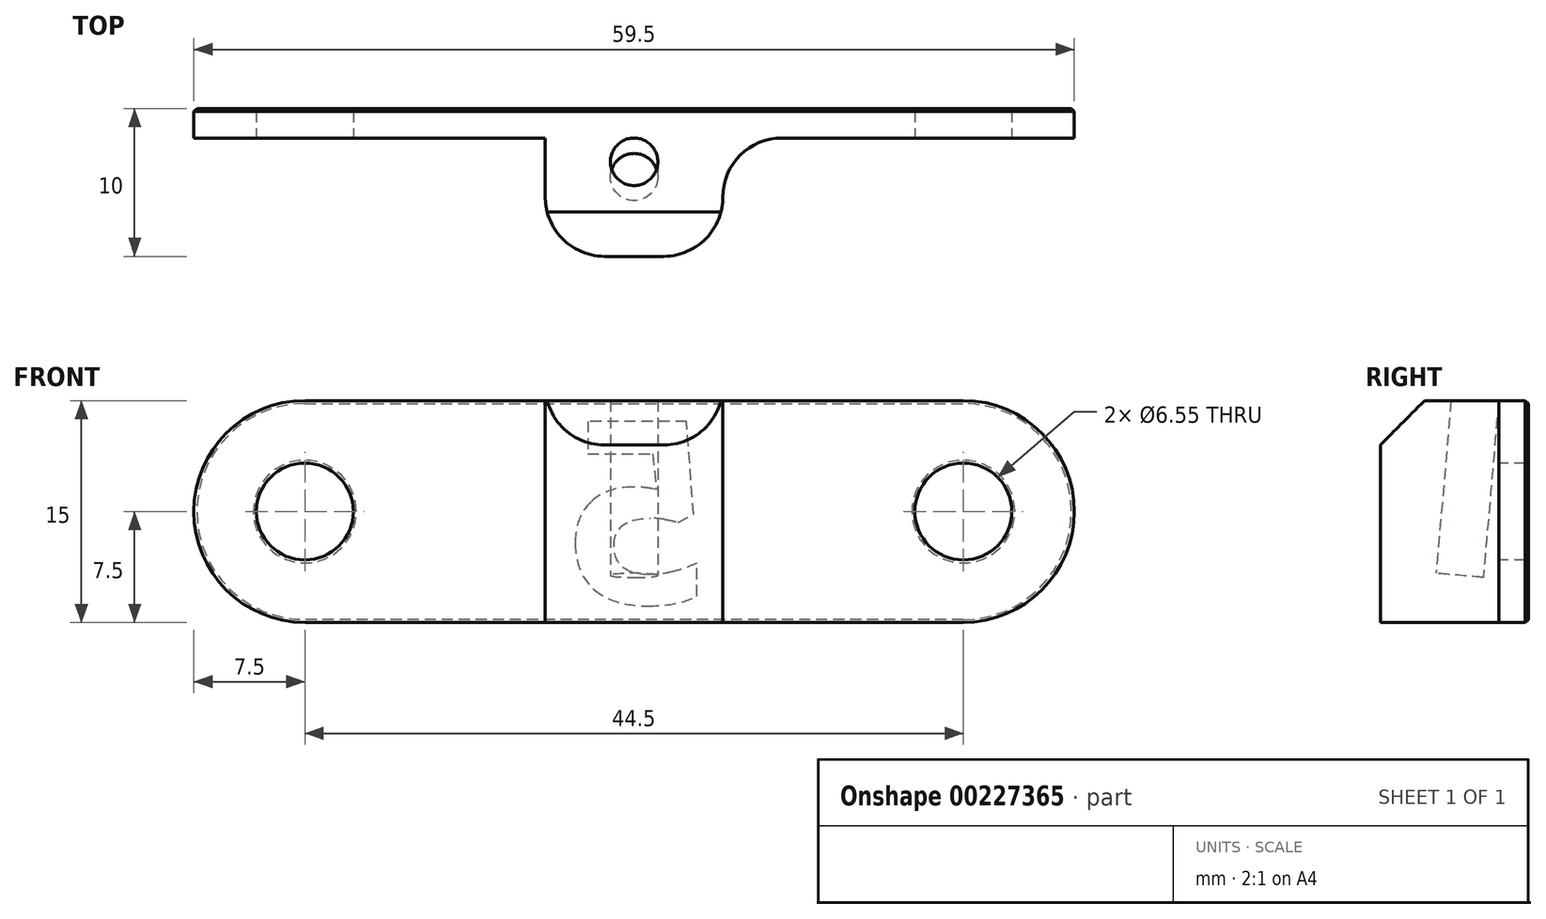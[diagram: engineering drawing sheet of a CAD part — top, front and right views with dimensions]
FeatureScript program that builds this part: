
annotation { "Feature Type Name" : "Feature", "Feature Type Description" : "" }
export const myFeature = defineFeature(function(context is Context, id is Id, definition is map)
    precondition{}
    {
        {
            var Q0;
            Q0=qCreatedBy(makeId("Front.planeOp"),FACE);
            var sketch = newSketch(context, id + "F0", { "sketchPlane" : qUnion([Q0])});
            skCircle(sketch, "E0", {"center": v(-22.25, 0) * mm, "radius": 3.28 * mm});
            skCircle(sketch, "E1", {"center": v(22.25, 0) * mm, "radius": 3.28 * mm});
            skLineSegment(sketch, "E2", {"start": v(-22.25, 0) * mm, "end": v(22.25, 0) * mm, "construction": true});
            skArc(sketch, "E3.0.startCap", {"start": v(-22.25, -7.5) * mm, "mid": v(-29.75, 0) * mm, "end": v(-22.25, 7.5) * mm});
            skArc(sketch, "E3.0.endCap", {"start": v(22.25, 7.5) * mm, "mid": v(29.75, 0) * mm, "end": v(22.25, -7.5) * mm});
            skLineSegment(sketch, "E3.0.left", {"start": v(-22.25, 7.5) * mm, "end": v(22.25, 7.5) * mm});
            skLineSegment(sketch, "E3.0.right", {"start": v(-22.25, -7.5) * mm, "end": v(22.25, -7.5) * mm});
            skSolve(sketch);
        }
        {
            var Q0;
            Q0=qSketchRegion(id+"F0",true);
            extrude(context, id + "F1", {"entities" : qUnion([Q0]), "oppositeDirection" : true, "depth" : 2 * mm, "offsetDistance" : 25 * mm});
        }
        {
            var Q0;
            Q0=qCreatedBy(makeId("Right.planeOp"),FACE);
            var sketch = newSketch(context, id + "F2", { "sketchPlane" : qUnion([Q0])});
            skLineSegment(sketch, "E4", {"start": v(-1.05, -4.45) * mm, "end": v(3, 41.76) * mm});
            skLineSegment(sketch, "E5", {"start": v(3, 41.76) * mm, "end": v(-0.2, 42.04) * mm});
            skLineSegment(sketch, "E6", {"start": v(-0.2, 42.04) * mm, "end": v(-4.23, -4.18) * mm});
            skLineSegment(sketch, "E7", {"start": v(-4.23, -4.18) * mm, "end": v(-1.05, -4.45) * mm});
            skLineSegment(sketch, "E8.0.0", {"start": v(0, -7.5) * mm, "end": v(0, 7.5) * mm, "construction": true});
            skLineSegment(sketch, "E8.0.2", {"start": v(0, -7.5) * mm, "end": v(0, 7.5) * mm, "construction": true});
            skLineSegment(sketch, "E9", {"start": v(1.4, 41.9) * mm, "end": v(-2.64, -4.31) * mm});
            skSolve(sketch);
        }
        {
            var Q0;
            Q0=qCreatedBy(makeId("Right.planeOp"),FACE);
            var sketch = newSketch(context, id + "F3", { "sketchPlane" : qUnion([Q0])});
            skLineSegment(sketch, "E10.0.0", {"start": v(0, -7.5) * mm, "end": v(0, 7.5) * mm, "construction": true});
            skLineSegment(sketch, "E10.0.2", {"start": v(0, -7.5) * mm, "end": v(0, 7.5) * mm, "construction": true});
            skLineSegment(sketch, "E11.bottom", {"start": v(0, 7.5) * mm, "end": v(-8, 7.5) * mm});
            skLineSegment(sketch, "E11.top", {"start": v(0, -7.5) * mm, "end": v(-8, -7.5) * mm});
            skLineSegment(sketch, "E11.left", {"start": v(0, 7.5) * mm, "end": v(0, -7.5) * mm});
            skLineSegment(sketch, "E11.right", {"start": v(-8, 7.5) * mm, "end": v(-8, -7.5) * mm});
            skSolve(sketch);
        }
        {
            var Q0;
            Q0=qSketchRegion(id+"F3",true);
            extrude(context, id + "F4", {"entities" : qUnion([Q0]), "operationType" : NewBodyOperationType.ADD, "endBound" : BoundingType.SYMMETRIC, "depth" : 12 * mm, "offsetDistance" : 25 * mm});
        }
        {
            var Q0;
            Q0=makeQuery(id+"F4.opExtrude","SWEPT_EDGE",EDGE,{"disambiguationData":[OSD([sQuery(id+"F3.wireOp",EDGE,"E11.bottom"),sQuery(id+"F3.wireOp",EDGE,"E11.right")])]});
            chamfer(context, id + "F5", {"entities" : qUnion([Q0]), "width" : 3 * mm});
        }
        {
            var Q0;
            Q0=makeQuery(id+"F4.opExtrude","SWEPT_EDGE",EDGE,{"disambiguationData":[OSD([sQuery(id+"F3.wireOp",EDGE,"E11.top"),sQuery(id+"F3.wireOp",EDGE,"E11.left")])]});
            var Q1;
            Q1=makeQuery(id+"F4.opExtrude","CAP_EDGE",EDGE,{"disambiguationData":[OSD([sQuery(id+"F3.wireOp",EDGE,"E11.left")])],"isStart":false});
            var Q2;
            Q2=makeQuery(id+"F4.opExtrude","CAP_EDGE",EDGE,{"disambiguationData":[OSD([sQuery(id+"F3.wireOp",EDGE,"E11.left")])],"isStart":true});
            var Q3;
            Q3=makeQuery(id+"F4.opExtrude","CAP_EDGE",EDGE,{"disambiguationData":[OSD([sQuery(id+"F3.wireOp",EDGE,"E11.right")])],"isStart":false});
            var Q4;
            Q4=makeQuery(id+"F4.opExtrude","CAP_EDGE",EDGE,{"disambiguationData":[OSD([sQuery(id+"F3.wireOp",EDGE,"E11.right")])],"isStart":true});
            fillet(context, id + "F6", {"entities" : qUnion([Q0, Q1, Q2, Q3, Q4]), "radius" : 4 * mm, "allowEdgeOverflow" : false});
        }
        {
            var Q0;
            {var subQ0=sQuery(id+"F2.wireOp",EDGE,"E6");Q0=makeQuery(id+"F2.imprint","IMPRINT",FACE,{"disambiguationData":[TD([[makeQuery(id+"F2.imprint","IMPRINT",EDGE,{"derivedFrom":subQ0}),1.0]])]});}
            var Q1;
            Q1=sQuery(id+"F2.wireOp",EDGE,"E9");
            revolve(context, id + "F7", {"operationType" : NewBodyOperationType.REMOVE, "entities" : qUnion([Q0]), "axis" : qUnion([Q1]), "revolveType" : RevolveType.FULL, "oppositeDirection" : true});
        }
        {
            var Q0;
            Q0=makeQuery(id+"F1.opExtrude","CAP_FACE",FACE,{"disambiguationData":[OSD([sQuery(id+"F0.wireOp",EDGE,"E0"),sQuery(id+"F0.wireOp",EDGE,"E1"),sQuery(id+"F0.wireOp",EDGE,"E3.0.startCap"),sQuery(id+"F0.wireOp",EDGE,"E3.0.endCap"),sQuery(id+"F0.wireOp",EDGE,"E3.0.left"),sQuery(id+"F0.wireOp",EDGE,"E3.0.right")])],"isStart":false});
            chamfer(context, id + "F8", {"entities" : qUnion([Q0]), "width" : 0.2 * mm});
        }
        {
            var Q0;
            Q0=makeQuery(id+"F1.opExtrude","CAP_FACE",FACE,{"disambiguationData":[OSD([sQuery(id+"F0.wireOp",EDGE,"E0"),sQuery(id+"F0.wireOp",EDGE,"E1"),sQuery(id+"F0.wireOp",EDGE,"E3.0.startCap"),sQuery(id+"F0.wireOp",EDGE,"E3.0.endCap"),sQuery(id+"F0.wireOp",EDGE,"E3.0.left"),sQuery(id+"F0.wireOp",EDGE,"E3.0.right")])],"isStart":false});
            var sketch = newSketch(context, id + "F9", { "sketchPlane" : qUnion([Q0])});
            skText(sketch, "E12", { "text": "5", "fontName": "OpenSans-Bold.ttf"});
            const initialGuessF9  = {"E12": [-0.0051, -0.00621, 1, 0, 0.01242]};
            skSetInitialGuess(sketch, initialGuessF9);
            skSolve(sketch);
        }
        {
            var Q0;
            Q0=qSketchRegion(id+"F9",true);
            extrude(context, id + "F10", {"entities" : qUnion([Q0]), "operationType" : NewBodyOperationType.REMOVE, "oppositeDirection" : true, "depth" : 0.2 * mm, "offsetDistance" : 25 * mm});
        }
    });
